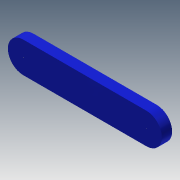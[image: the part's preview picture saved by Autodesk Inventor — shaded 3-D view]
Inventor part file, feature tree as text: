
AUTODESK INVENTOR PART (.ipt)
format: ipt  version: 2013 (Build 170138000, 138)  size: 107,520 bytes
history: native  units: mm
features: extrude x4, sketch x4
ambient origin geometry x8: Origin, YZ Plane, XZ Plane, XY Plane, X Axis, Y Axis, Z Axis, Center Point
bodies: Solid1 (feature_tree)
feature tree (8):
  extrude  "Extrusion1"  Depth=6.0mm
  extrude  "Extrusion2"  Depth=6.0mm
  extrude  "Extrusion3"  Depth=2.0mm
  extrude  "Extrusion4"  Depth=3.0mm
  sketch  "Sketch1"  dims[d0=24.0mm d1=6.0mm]
  sketch  "Sketch2"  dims[d2=6.0mm d3=6.0mm]
  sketch  "Sketch3"  dims[d4=2.0mm d5=0.0mm d6=2.0mm]
  sketch  "Sketch4"  dims[d7=3.0mm d8=3.0mm d9=2.0mm d10=0.0mm d11=0.01mm d12=0.01mm d13=2.0mm d14=0.0mm d15=0.1mm d16=0.1mm d17=2.0mm d18=0.0mm]
